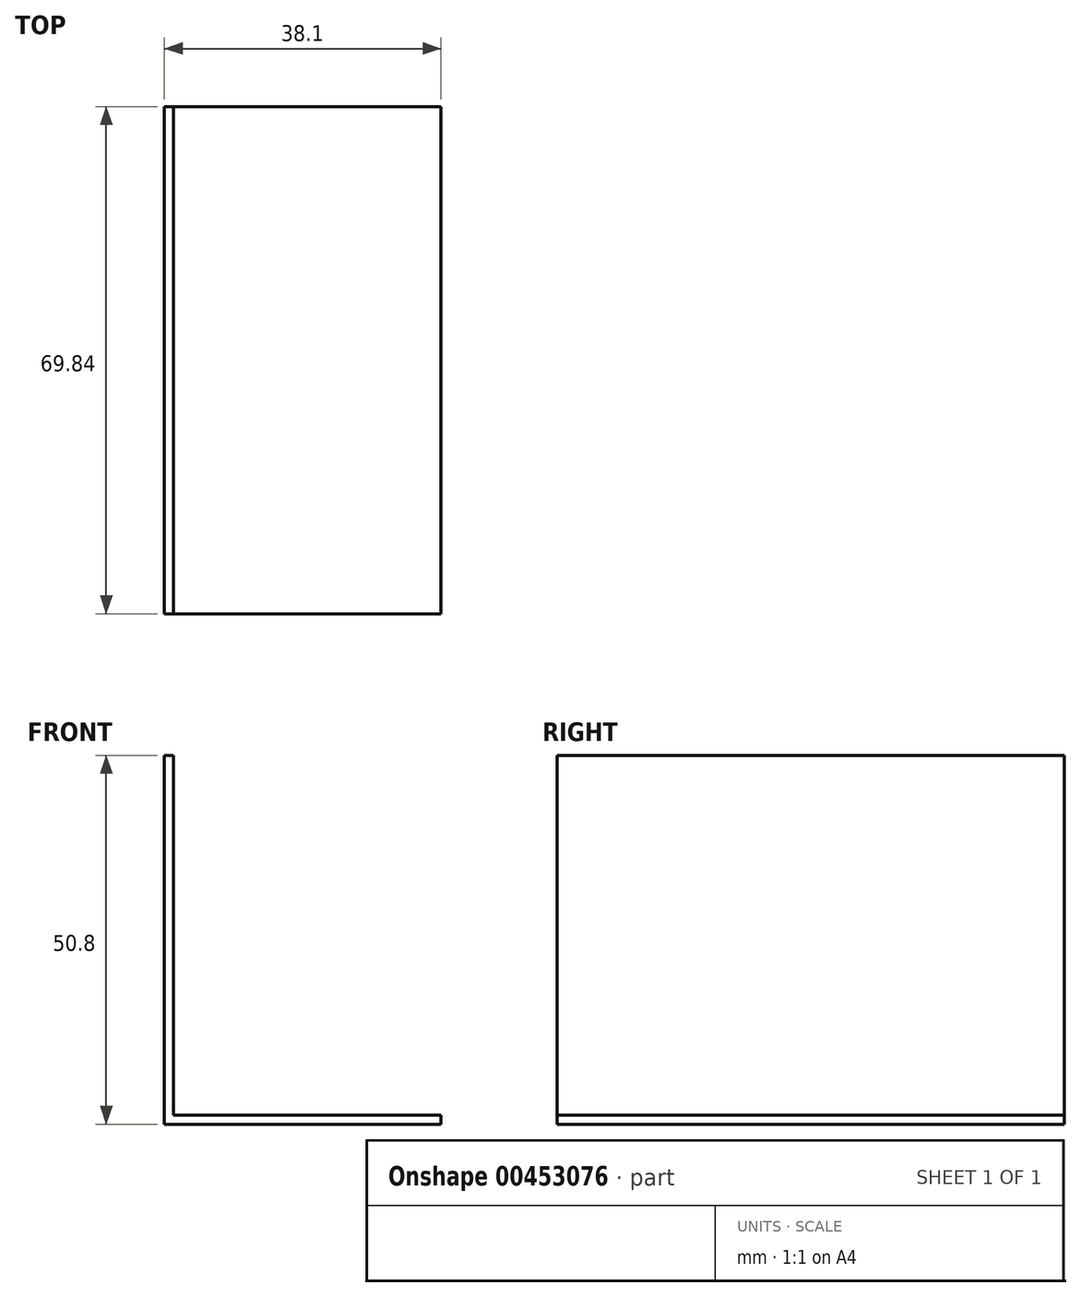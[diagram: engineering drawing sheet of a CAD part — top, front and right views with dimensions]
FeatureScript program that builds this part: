
annotation { "Feature Type Name" : "Feature", "Feature Type Description" : "" }
export const myFeature = defineFeature(function(context is Context, id is Id, definition is map)
    precondition{}
    {
        {
            var Q0;
            Q0=qCreatedBy(makeId("Front.planeOp"),FACE);
            var sketch = newSketch(context, id + "F0", { "sketchPlane" : qUnion([Q0])});
            skLineSegment(sketch, "E0", {"start": v(0, 0) * mm, "end": v(0, 50.8) * mm});
            skLineSegment(sketch, "E1", {"start": v(0, 0) * mm, "end": v(38.1, 0) * mm});
            skLineSegment(sketch, "E2", {"start": v(0, 50.8) * mm, "end": v(1.27, 50.8) * mm});
            skLineSegment(sketch, "E3", {"start": v(1.27, 50.8) * mm, "end": v(1.27, 1.27) * mm});
            skLineSegment(sketch, "E4", {"start": v(1.27, 1.27) * mm, "end": v(38.1, 1.27) * mm});
            skLineSegment(sketch, "E5", {"start": v(38.1, 1.27) * mm, "end": v(38.1, 0) * mm});
            skSolve(sketch);
        }
        {
            var Q0;
            Q0 = qSketchRegion(id + "F0", true);
            extrude(context, id + "F1", {"entities" : qUnion([Q0]), "depth" : 34.92 * mm, "offsetDistance" : 25.4 * mm, "hasSecondDirection" : true, "secondDirectionOppositeDirection" : true, "secondDirectionDepth" : 34.92 * mm});
        }
    });
